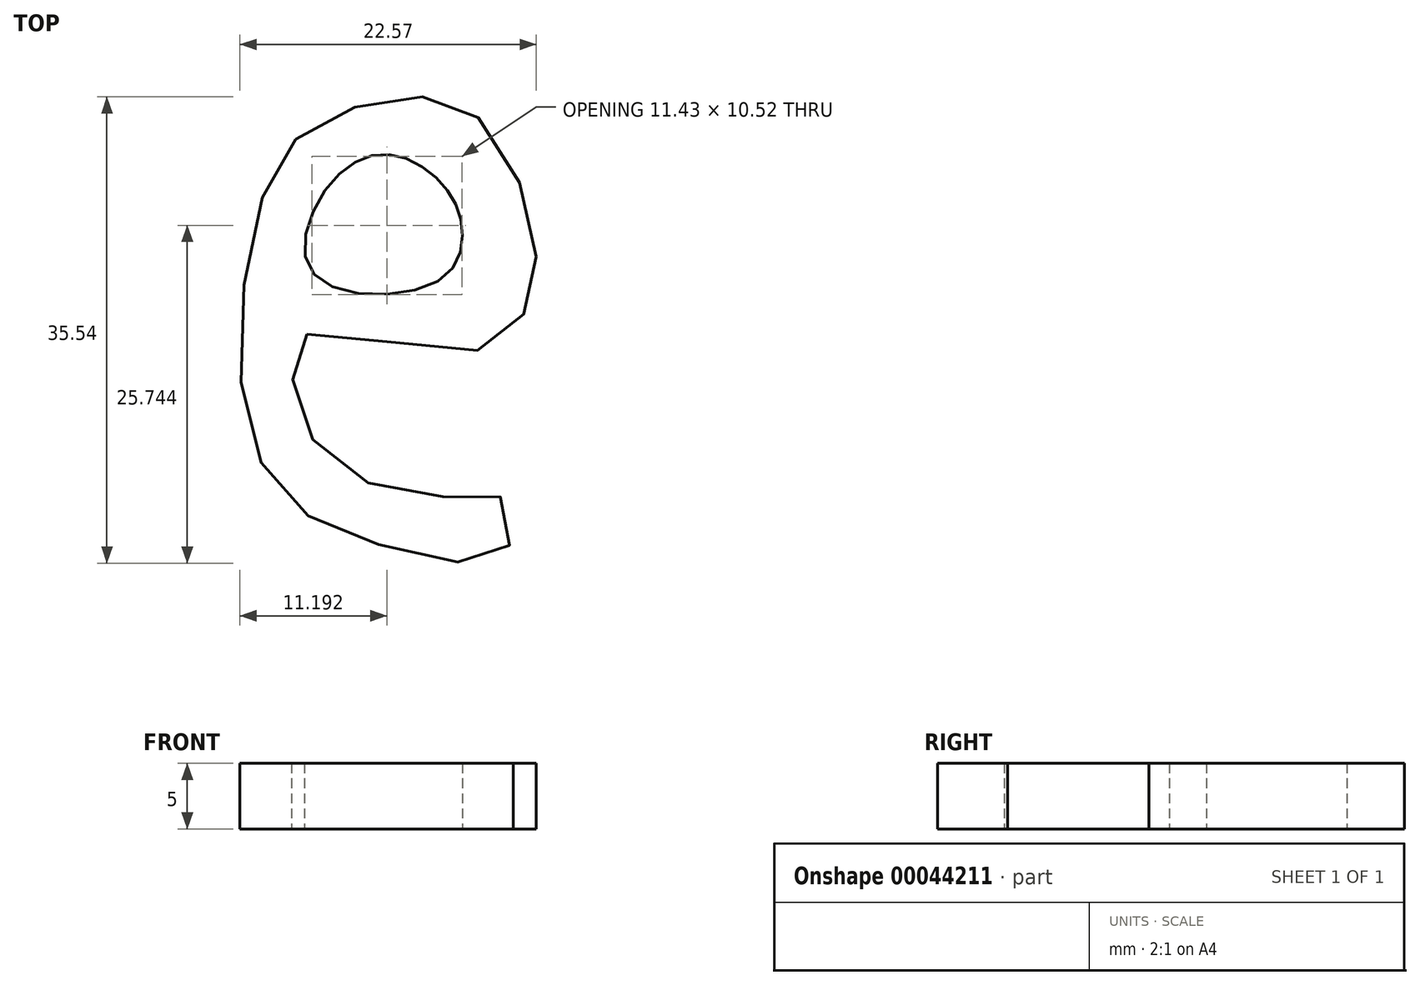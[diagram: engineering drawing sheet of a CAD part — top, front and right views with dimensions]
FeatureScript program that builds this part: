
annotation { "Feature Type Name" : "Feature", "Feature Type Description" : "" }
export const myFeature = defineFeature(function(context is Context, id is Id, definition is map)
    precondition{}
    {
        {
            var Q0;
            Q0=qCreatedBy(makeId("Top.planeOp"),FACE);
            var sketch = newSketch(context, id + "F0", { "sketchPlane" : qUnion([Q0])});
            skFitSpline(sketch, "E0", {"points": [v(-45.99, 26.76) * mm, v(-36.58, 26.22) * mm, v(-34.7, 30.26) * mm, v(-36.3, 33.75) * mm, v(-40.34, 35.9) * mm, v(-44.91, 33.48) * mm, v(-45.99, 26.76) * mm]});
            skFitSpline(sketch, "E1", {"points": [v(-46.53, 22.19) * mm, v(-34.42, 20.84) * mm, v(-29.85, 24.07) * mm, v(-29.31, 30.26) * mm, v(-33.62, 38.86) * mm, v(-39.27, 40.2) * mm, v(-46.53, 37.79) * mm, v(-50.3, 31.33) * mm, v(-51.37, 17.08) * mm, v(-47.33, 9) * mm, v(-38.46, 5.51) * mm, v(-31.47, 5.51) * mm, v(-31.47, 9.55) * mm, v(-36.58, 9.82) * mm, v(-44.91, 12.77) * mm, v(-47.6, 18.7) * mm, v(-46.53, 22.19) * mm]});
            skSolve(sketch);
        }
        {
            var Q0;
            Q0=makeQuery(id+"F0.imprint","IMPRINT",FACE,{"disambiguationData":[TD([[makeQuery(id+"F0.imprint","IMPRINT",EDGE,{"derivedFrom":sQuery(id+"F0.wireOp",EDGE,"E0")}),-1.0]])]});
            extrude(context, id + "F1", {"entities" : qUnion([Q0]), "depth" : 5 * mm});
        }
    });
